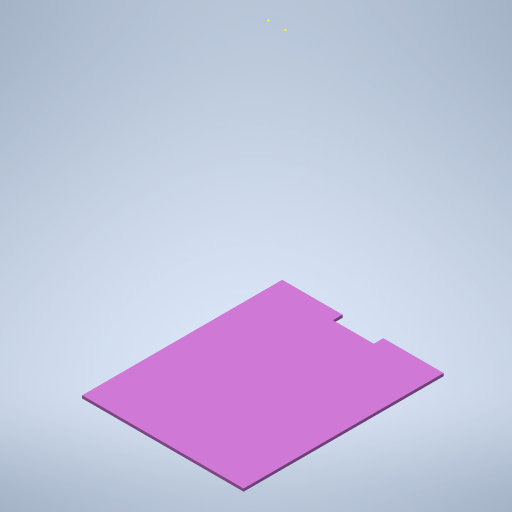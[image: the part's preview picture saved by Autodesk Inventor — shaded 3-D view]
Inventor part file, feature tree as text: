
AUTODESK INVENTOR PART (.ipt)
format: ipt  version: 2024 (Build 280153000, 153)  size: 756,224 bytes
history: native  units: mm
features: sketch x16, extrude x13, fillet x8, plane x4, other x2, projected_geometry x2, split x1
ambient origin geometry x8: Origin, YZ Plane, XZ Plane, XY Plane, X Axis, Y Axis, Z Axis, Center Point
bodies: Solid1 (feature_tree)
feature tree (46):
  extrude  "Extrusion1"  Depth=77.5mm
  extrude  "Extrusion2"  Depth=15.0mm
  sketch  "Sketch3"  dims[d5=90.0mm d6=0.0mm d7=60.0mm d8=0.0mm d9=50.0mm d11=80.0mm d12=90.0mm d13=0.0mm d14=10.0mm]
  extrude  "Extrusion3"  Depth=60.0mm TaperAngle=0.0deg
  fillet  "Fillet1"  Radius=50.0mm
  fillet  "Fillet2"  Radius=80.0mm
  fillet  "Fillet3"  Radius=90.0mm
  fillet  "Fillet4"  Radius=10.0mm
  plane  "Work Plane1"
  extrude  "Extrusion4"  Depth=3.0mm
  extrude  "Extrusion5"  [1 undecoded]
  fillet  "Fillet5"  Radius=20.0mm
  fillet  "Fillet6"  Radius=20.0mm
  plane  "Work Plane2"
  extrude  "Extrusion6"  Depth=20.0mm
  fillet  "Fillet7"  Radius=50.0mm
  plane  "Work Plane3"
  split  "Split1"
  sketch  "Sketch8"  dims[d28=81.25mm d29=10.0mm d30=0.0mm]
  extrude  "Extrusion7"  Depth=7.0mm
  extrude  "Extrusion8"  Depth=10.0mm TaperAngle=0.0deg
  extrude  "Extrusion10"  [1 undecoded]
  extrude  "Extrusion11"  Depth=5.0mm
  sketch  "Sketch14"  dims[d50=8.0mm d51=8.0mm]
  extrude  "Extrusion12"  Depth=5.0mm
  other  "Lip1"
  fillet  "Fillet12"  Radius=20.0mm
  plane  "Plano de trabajo4"
  extrude  "Extrusión14"  Depth=52.0mm TaperAngle=0.0deg
  extrude  "Extrusión15"  Depth=8.0mm
  sketch  "Sketch1"  dims[d0=73.0mm d1=77.5mm]
  sketch  "Sketch2"  dims[d3=10.0mm d4=15.0mm]
  projected_geometry  "Projected Loop1"
  sketch  "Sketch4"  dims[d15=5.0mm d16=3.0mm]
  sketch  "Sketch5"  dims[d17=10.0mm d18=-39.5mm d19=20.0mm d20=20.0mm]
  sketch  "Sketch6"  dims[d21=50.0mm d22=0.0mm d23=20.0mm d24=50.0mm d25=0.0mm]
  sketch  "Sketch7"  dims[d26=10.0mm d27=7.0mm]
  projected_geometry  "Projected Loop2"
  sketch  "Sketch9"  dims[d31=1.0mm d32=-60.75mm]
  sketch  "Sketch10"  dims[d33=10.0mm d34=0.0mm d38=5.0mm]
  sketch  "Sketch12"  dims[d39=10.0mm d40=5.0mm d41=20.0mm]
  sketch  "Sketch13"  dims[d42=10.0mm d43=0.0mm d48=52.0mm d49=0.0mm]
  sketch  "Sketch15"  dims[d52=10.0mm d53=0.0mm]
  sketch  "Boceto18"  dims[d55=30.0mm d56=0.0mm]
  other  "Sólido3"
  sketch  "Boceto19"  dims[d57=1.0mm d58=1.0mm d59=0.0mm d60=0.0mm d61=0.0mm d62=0.0mm d64=5.0mm d65=-14.5mm d68=1.0mm d69=0.0mm d82=1.5mm d83=0.0mm d46=0.5mm d47=0.872665mm d84=0.5mm d85=0.872665mm]
note: 2 required parameter values undecoded (feature->parameter linkage not recoverable at this tier; creation-order binding heuristic only, values carry confidence <= 0.55)
